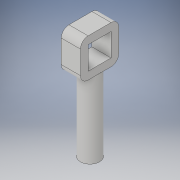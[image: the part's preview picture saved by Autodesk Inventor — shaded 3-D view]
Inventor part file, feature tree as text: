
AUTODESK INVENTOR PART (.ipt)
format: ipt  version: 2019 (Build 230136000, 136)  size: 125,952 bytes
history: native  units: mm
features: extrude x2, sketch x2, fillet x1
ambient origin geometry x8: Origin, YZ Plane, XZ Plane, XY Plane, X Axis, Y Axis, Z Axis, Center Point
bodies: Solid1 (feature_tree)
feature tree (5):
  extrude  "Extrusion1"  Depth=6.0mm
  extrude  "Extrusion2"  Depth=10.0mm
  fillet  "Fillet1"  Radius=10.0mm
  sketch  "Sketch1"  dims[d0=6.0mm d1=6.0mm]
  sketch  "Sketch2"  dims[d2=2.0mm d3=10.0mm d4=10.0mm d5=2.0mm d6=5.0mm d7=0.0mm d8=5.0mm d9=5.0mm d10=2.5mm d11=20.0mm d12=0.0mm d13=2.0mm]
